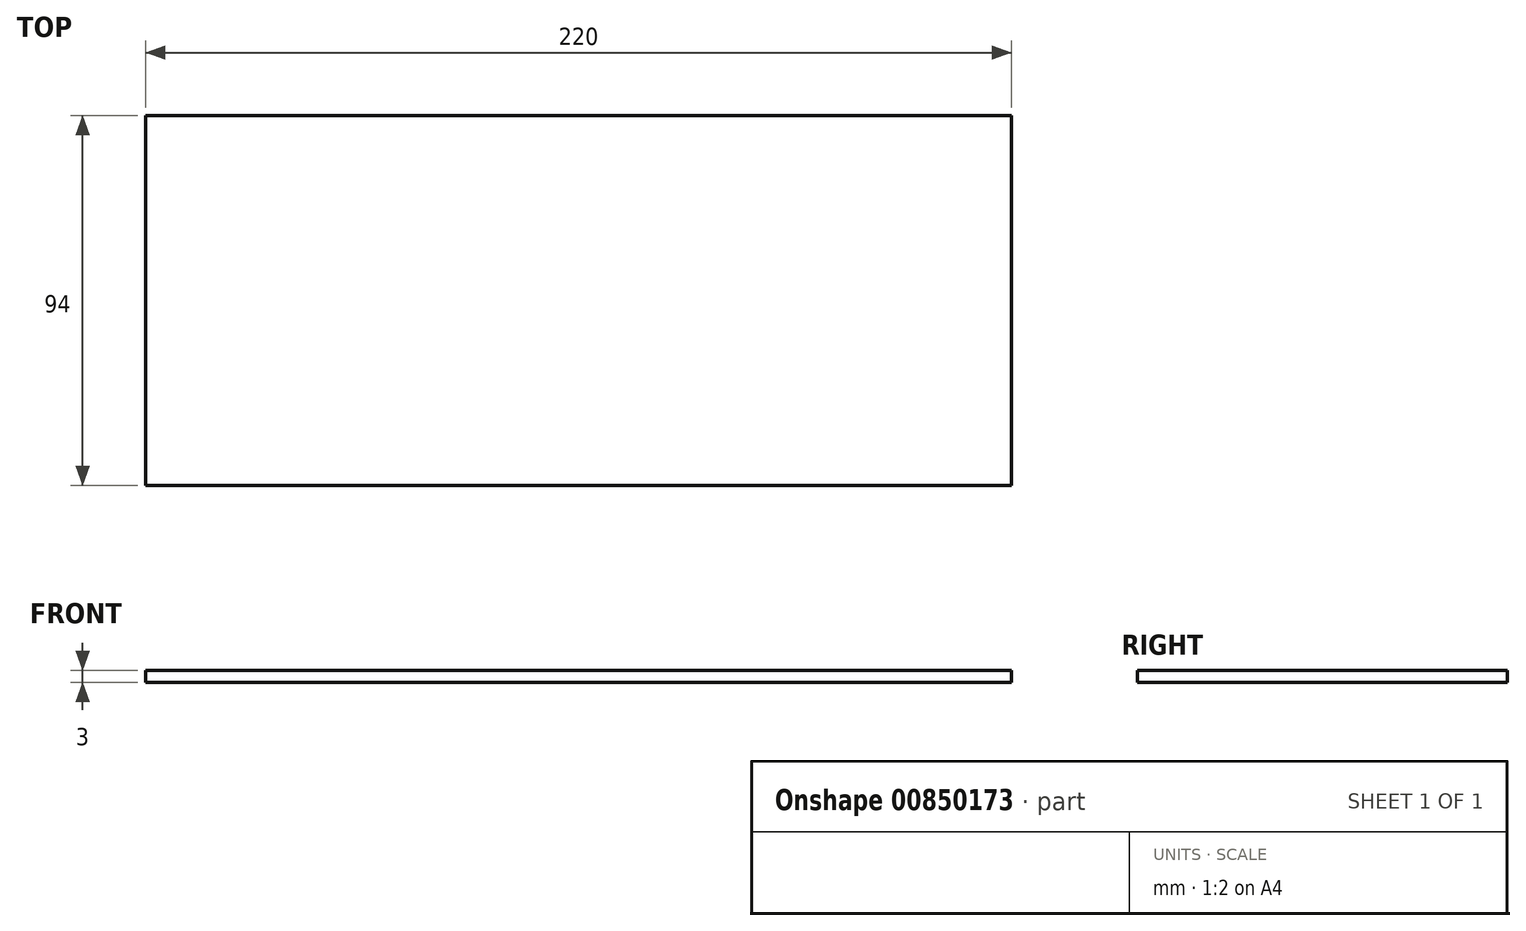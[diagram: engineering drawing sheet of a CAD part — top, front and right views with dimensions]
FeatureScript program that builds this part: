
annotation { "Feature Type Name" : "Feature", "Feature Type Description" : "" }
export const myFeature = defineFeature(function(context is Context, id is Id, definition is map)
    precondition{}
    {
        {
            var Q0;
            Q0=qCreatedBy(makeId("Top.planeOp"),FACE);
            var sketch = newSketch(context, id + "F0", { "sketchPlane" : qUnion([Q0])});
            skLineSegment(sketch, "E0.bottom", {"start": v(-110, 47) * mm, "end": v(110, 47) * mm});
            skLineSegment(sketch, "E0.top", {"start": v(-110, -47) * mm, "end": v(110, -47) * mm});
            skLineSegment(sketch, "E0.left", {"start": v(-110, 47) * mm, "end": v(-110, -47) * mm});
            skLineSegment(sketch, "E0.right", {"start": v(110, 47) * mm, "end": v(110, -47) * mm});
            skSolve(sketch);
        }
        {
            var Q0;
            Q0 = qSketchRegion(id + "F0", true);
            extrude(context, id + "F1", {"entities" : qUnion([Q0]), "depth" : 3 * mm, "offsetDistance" : 25 * mm});
        }
    });
